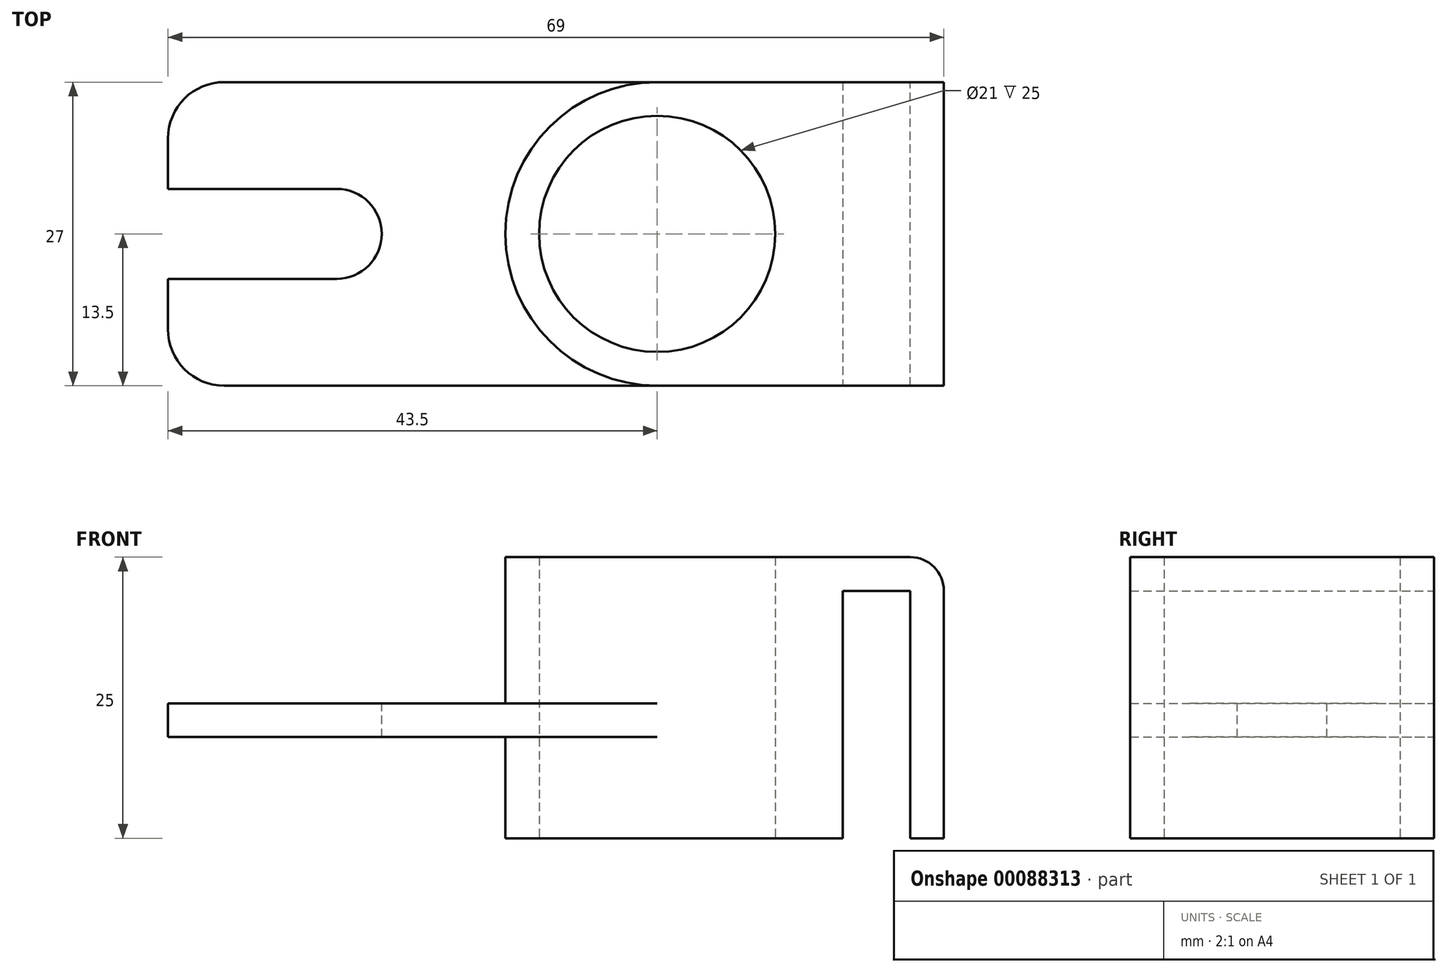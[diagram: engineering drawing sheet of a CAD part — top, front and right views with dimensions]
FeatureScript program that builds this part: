
annotation { "Feature Type Name" : "Feature", "Feature Type Description" : "" }
export const myFeature = defineFeature(function(context is Context, id is Id, definition is map)
    precondition{}
    {
        {
            var Q0;
            Q0=qCreatedBy(makeId("Top.planeOp"),FACE);
            var sketch = newSketch(context, id + "F0", { "sketchPlane" : qUnion([Q0])});
            skCircle(sketch, "E0", {"center": v(0, 0) * mm, "radius": 10.5 * mm});
            skCircle(sketch, "E1", {"center": v(0, 0) * mm, "radius": 13.5 * mm});
            skLineSegment(sketch, "E2", {"start": v(0, 13.5) * mm, "end": v(25.5, 13.5) * mm});
            skLineSegment(sketch, "E3", {"start": v(25.5, 13.5) * mm, "end": v(25.5, -13.5) * mm});
            skLineSegment(sketch, "E4", {"start": v(0, -13.5) * mm, "end": v(25.5, -13.5) * mm});
            skLineSegment(sketch, "E5", {"start": v(13.5, 0) * mm, "end": v(13.5, 13.5) * mm});
            skLineSegment(sketch, "E6", {"start": v(13.5, 0) * mm, "end": v(13.5, -13.5) * mm});
            skLineSegment(sketch, "E7", {"start": v(16.5, 13.5) * mm, "end": v(16.5, -13.5) * mm, "construction": true});
            skLineSegment(sketch, "E8", {"start": v(22.5, 13.5) * mm, "end": v(22.5, -13.5) * mm, "construction": true});
            skLineSegment(sketch, "E9", {"start": v(16.5, 13.5) * mm, "end": v(16.5, -13.5) * mm});
            skLineSegment(sketch, "E10", {"start": v(22.5, -13.5) * mm, "end": v(22.5, 13.5) * mm});
            skSolve(sketch);
        }
        {
            var Q0;
            Q0=qSketchRegion(id+"F0",true);
            extrude(context, id + "F1", {"entities" : qUnion([Q0]), "depth" : 3 * mm});
        }
        {
            var Q0;
            Q0=makeQuery(id+"F0.imprint","IMPRINT",FACE,{"disambiguationData":[TD([[makeQuery(id+"F0.imprint","IMPRINT",EDGE,{"derivedFrom":sQuery(id+"F0.wireOp",EDGE,"E0")}),-1.0]])]});
            var Q1;
            {var subQ3=sQuery(id+"F0.wireOp",EDGE,"E5");Q1=makeQuery(id+"F0.imprint","IMPRINT",FACE,{"disambiguationData":[TD([[makeQuery(id+"F0.imprint","IMPRINT",EDGE,{"derivedFrom":subQ3}),1.0]])]});}
            var Q2;
            {var subQ1=sQuery(id+"F0.wireOp",EDGE,"E5");Q2=makeQuery(id+"F0.imprint","IMPRINT",FACE,{"disambiguationData":[TD([[makeQuery(id+"F0.imprint","IMPRINT",EDGE,{"derivedFrom":subQ1}),-1.0]])]});}
            var Q3;
            {var subQ0=sQuery(id+"F0.wireOp",EDGE,"E3");Q3=makeQuery(id+"F0.imprint","IMPRINT",FACE,{"disambiguationData":[TD([[makeQuery(id+"F0.imprint","IMPRINT",EDGE,{"derivedFrom":subQ0}),-1.0]])]});}
            var Q4;
            {var subQ3=sQuery(id+"F0.wireOp",EDGE,"E6");Q4=makeQuery(id+"F0.imprint","IMPRINT",FACE,{"disambiguationData":[TD([[makeQuery(id+"F0.imprint","IMPRINT",EDGE,{"derivedFrom":subQ3}),-1.0]])]});}
            extrude(context, id + "F2", {"entities" : qUnion([Q0, Q1, Q2, Q3, Q4]), "operationType" : NewBodyOperationType.ADD, "oppositeDirection" : true, "depth" : 22 * mm});
        }
        {
            var Q0;
            Q0=makeQuery(id+"F2.opExtrude","CAP_EDGE",EDGE,{"disambiguationData":[OSD([sQuery(id+"F0.wireOp",EDGE,"E9")])],"isStart":true});
            var Q1;
            Q1=makeQuery(id+"F2.opExtrude","CAP_EDGE",EDGE,{"disambiguationData":[OSD([sQuery(id+"F0.wireOp",EDGE,"E10")])],"isStart":true});
            var Q2;
            Q2=makeQuery(id+"F1.opExtrude","CAP_EDGE",EDGE,{"disambiguationData":[OSD([sQuery(id+"F0.wireOp",EDGE,"E3")])],"isStart":false});
            fillet(context, id + "F3", {"entities" : qUnion([Q0, Q1, Q2]), "radius" : 3 * mm, "tangentPropagation" : true, "allowEdgeOverflow" : false});
        }
        {
            var Q0;
            Q0=makeQuery(id+"F2.opExtrude","CAP_FACE",FACE,{"disambiguationData":[OSD([sQuery(id+"F0.wireOp",EDGE,"E0"),sQuery(id+"F0.wireOp",EDGE,"E1"),sQuery(id+"F0.wireOp",EDGE,"E2"),sQuery(id+"F0.wireOp",EDGE,"E4"),sQuery(id+"F0.wireOp",EDGE,"E9")])],"isStart":false});
            cPlane(context, id + "F4", {"entities" : qUnion([Q0]), "cplaneType" : CPlaneType.OFFSET, "offset" : 12 * mm, "oppositeDirection" : true, "width" : 150 * mm, "height" : 150 * mm});
        }
        {
            var Q0;
            Q0=qCreatedBy(id+"F4.planeOp",FACE);
            var sketch = newSketch(context, id + "F5", { "sketchPlane" : qUnion([Q0])});
            skCircle(sketch, "E11.0", {"center": v(0, 0) * mm, "radius": 10.5 * mm});
            skArc(sketch, "E12.0.0", {"start": v(0, 13.5) * mm, "mid": v(-13.5, 0) * mm, "end": v(0, -13.5) * mm});
            skLineSegment(sketch, "E12.0.1", {"start": v(0, -13.5) * mm, "end": v(16.5, -13.5) * mm});
            skLineSegment(sketch, "E12.0.2", {"start": v(16.5, -13.5) * mm, "end": v(16.5, 13.5) * mm});
            skLineSegment(sketch, "E12.0.3", {"start": v(16.5, 13.5) * mm, "end": v(0, 13.5) * mm});
            skLineSegment(sketch, "E13", {"start": v(0, -13.5) * mm, "end": v(-43.5, -13.5) * mm});
            skLineSegment(sketch, "E14", {"start": v(-43.5, -13.5) * mm, "end": v(-43.5, -4) * mm});
            skLineSegment(sketch, "E15", {"start": v(-43.5, 13.5) * mm, "end": v(0, 13.5) * mm});
            skLineSegment(sketch, "E16.bottom", {"start": v(0, 0) * mm, "end": v(-28.5, 0) * mm, "construction": true});
            skLineSegment(sketch, "E16.top", {"start": v(0, 4) * mm, "end": v(-43.5, 4) * mm, "construction": true});
            skLineSegment(sketch, "E16.left", {"start": v(0, 0) * mm, "end": v(0, 4) * mm, "construction": true});
            skLineSegment(sketch, "E17.MirrorCS", {"start": v(0, -4) * mm, "end": v(-43.5, -4) * mm, "construction": true});
            skLineSegment(sketch, "E18", {"start": v(-43.5, 0) * mm, "end": v(-13.5, 0) * mm, "construction": true});
            skPoint(sketch, "E19", {"position": v(-28.5, 0) * mm});
            skArc(sketch, "E20", {"start": v(-28.5, -4) * mm, "mid": v(-24.5, 0) * mm, "end": v(-28.5, 4) * mm});
            skLineSegment(sketch, "E21", {"start": v(-28.5, 4) * mm, "end": v(-43.5, 4) * mm});
            skLineSegment(sketch, "E22", {"start": v(-43.5, -4) * mm, "end": v(-28.5, -4) * mm});
            skLineSegment(sketch, "E23.trimOffspring", {"start": v(-43.5, 4) * mm, "end": v(-43.5, 13.5) * mm});
            skSolve(sketch);
        }
        {
            var Q0;
            Q0=makeQuery(id+"F5.imprint","IMPRINT",FACE,{"disambiguationData":[TD([[makeQuery(id+"F5.imprint","IMPRINT",EDGE,{"derivedFrom":sQuery(id+"F5.wireOp",EDGE,"E11.0")}),-1.0]])]});
            extrude(context, id + "F6", {"entities" : qUnion([Q0]), "oppositeDirection" : true, "depth" : 12 * mm});
        }
        {
            var Q0;
            Q0=qSketchRegion(id+"F5",true);
            extrude(context, id + "F7", {"entities" : qUnion([Q0]), "operationType" : NewBodyOperationType.ADD, "depth" : 3 * mm});
        }
        {
            var Q0;
            Q0=makeQuery(id+"F7.opExtrude","SWEPT_EDGE",EDGE,{"disambiguationData":[OSD([sQuery(id+"F5.wireOp",EDGE,"E15"),sQuery(id+"F5.wireOp",EDGE,"E23.trimOffspring")])]});
            var Q1;
            Q1=makeQuery(id+"F7.opExtrude","SWEPT_EDGE",EDGE,{"disambiguationData":[OSD([sQuery(id+"F5.wireOp",EDGE,"E13"),sQuery(id+"F5.wireOp",EDGE,"E14")])]});
            fillet(context, id + "F8", {"entities" : qUnion([Q0, Q1]), "radius" : 5 * mm, "tangentPropagation" : true, "allowEdgeOverflow" : false});
        }
    });
